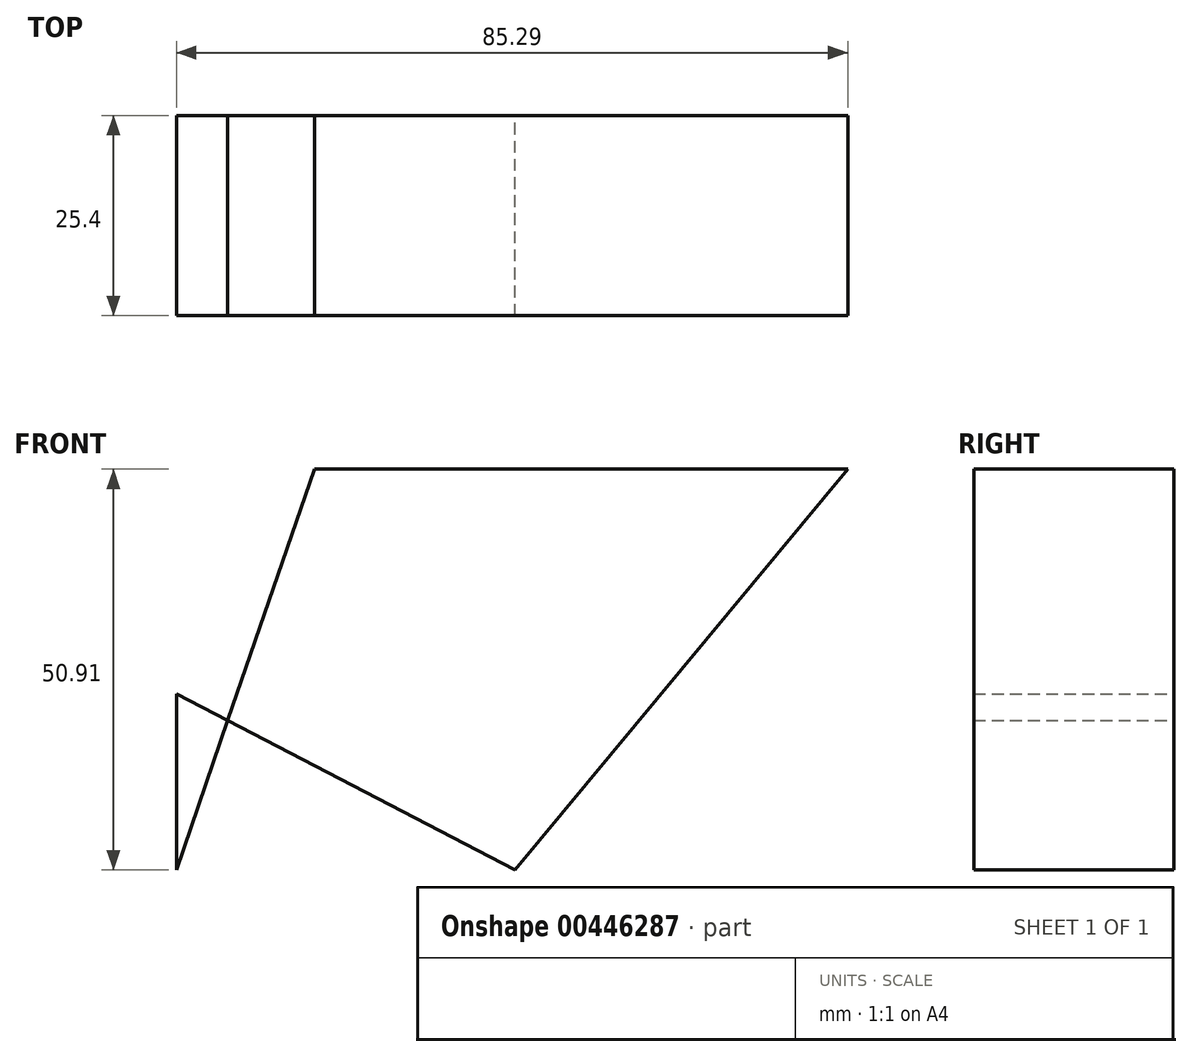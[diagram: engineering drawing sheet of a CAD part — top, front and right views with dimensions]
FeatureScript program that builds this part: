
annotation { "Feature Type Name" : "Feature", "Feature Type Description" : "" }
export const myFeature = defineFeature(function(context is Context, id is Id, definition is map)
    precondition{}
    {
        {
            var Q0;
            Q0=qCreatedBy(makeId("Front.planeOp"),FACE);
            var sketch = newSketch(context, id + "F0", { "sketchPlane" : qUnion([Q0])});
            skLineSegment(sketch, "E0", {"start": v(0, 0) * mm, "end": v(17.52, 50.9) * mm});
            skLineSegment(sketch, "E1", {"start": v(17.52, 50.9) * mm, "end": v(85.3, 50.9) * mm});
            skLineSegment(sketch, "E2", {"start": v(85.3, 50.9) * mm, "end": v(43.03, 0) * mm});
            skLineSegment(sketch, "E3", {"start": v(43.03, 0) * mm, "end": v(0, 22.37) * mm});
            skLineSegment(sketch, "E4", {"start": v(0, 22.37) * mm, "end": v(0, 0) * mm});
            skSolve(sketch);
        }
        {
            var Q0;
            Q0 = qSketchRegion(id + "F0", true);
            extrude(context, id + "F1", {"entities" : qUnion([Q0]), "depth" : 25.4 * mm});
        }
    });
